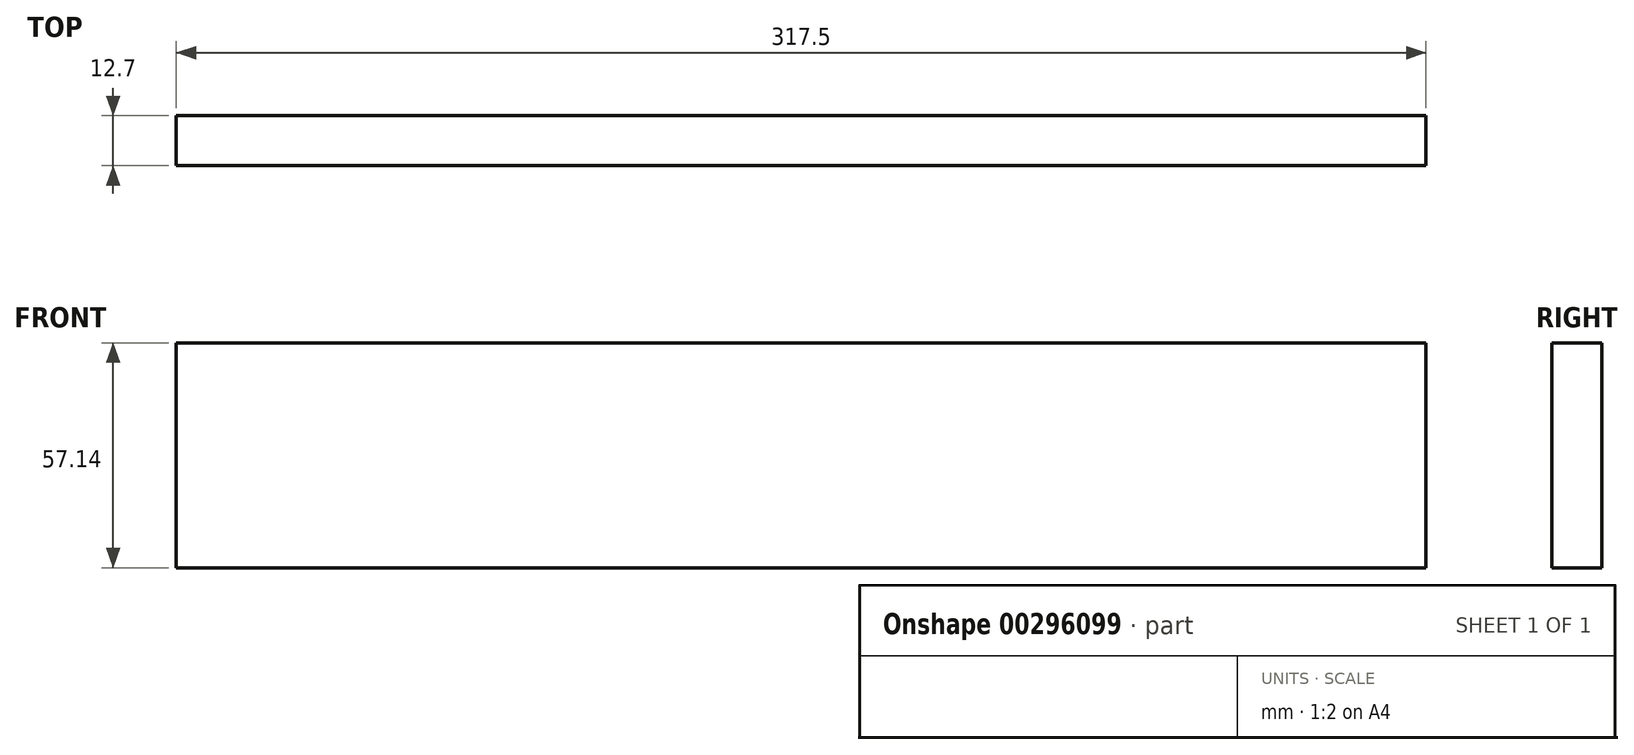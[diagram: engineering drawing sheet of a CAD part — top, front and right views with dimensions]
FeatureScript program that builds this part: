
annotation { "Feature Type Name" : "Feature", "Feature Type Description" : "" }
export const myFeature = defineFeature(function(context is Context, id is Id, definition is map)
    precondition{}
    {
        {
            var Q0;
            Q0=qCreatedBy(makeId("Front.planeOp"),FACE);
            var sketch = newSketch(context, id + "F0", { "sketchPlane" : qUnion([Q0])});
            skLineSegment(sketch, "E0.bottom", {"start": v(158.75, 28.57) * mm, "end": v(-158.75, 28.57) * mm});
            skLineSegment(sketch, "E0.top", {"start": v(158.75, -28.57) * mm, "end": v(-158.75, -28.58) * mm});
            skLineSegment(sketch, "E0.left", {"start": v(158.75, 28.58) * mm, "end": v(158.75, -28.57) * mm});
            skLineSegment(sketch, "E0.right", {"start": v(-158.75, 28.57) * mm, "end": v(-158.75, -28.58) * mm});
            skPoint(sketch, "E0.middle", {"position": v(0, 0) * mm});
            skSolve(sketch);
        }
        {
            var Q0;
            Q0=makeQuery(id+"F0.imprint","IMPRINT",FACE,{"disambiguationData":[TD([[makeQuery(id+"F0.imprint","IMPRINT",EDGE,{"derivedFrom":sQuery(id+"F0.wireOp",EDGE,"E0.bottom")}),1.0]])]});
            extrude(context, id + "F1", {"entities" : qUnion([Q0]), "depth" : 12.7 * mm});
        }
    });
